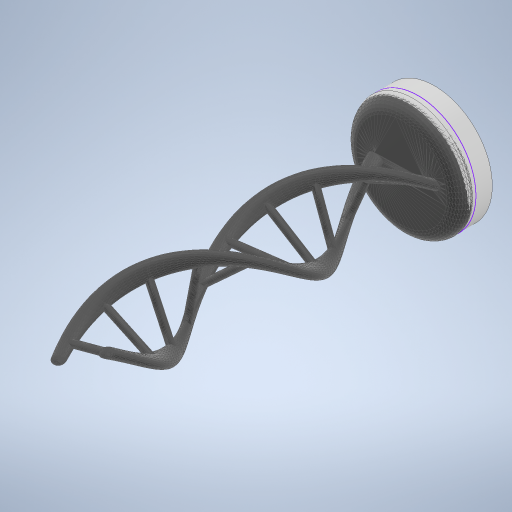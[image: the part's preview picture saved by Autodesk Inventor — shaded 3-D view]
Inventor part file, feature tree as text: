
AUTODESK INVENTOR PART (.ipt)
format: ipt  version: 2024.2 (Build 282272000, 272)  size: 821,248 bytes
history: native  units: mm
features: other x4, sketch x2, extrude x2, fillet x1
ambient origin geometry x8: Origin, YZ Plane, XZ Plane, XY Plane, X Axis, Y Axis, Z Axis, Center Point
bodies: Body1 (feature_tree)
feature tree (9):
  other  "Твердое тело1"
  other  "Double Helix DNA"
  sketch  "Эскиз1"
  extrude  "Выдавливание1"  Depth=10.0mm TaperAngle=0.0deg
  fillet  "Сопряжение1"  Radius=7.0mm
  other  "РабТочка1"
  extrude  "Выдавливание3"  Depth=3.0mm TaperAngle=0.0deg
  sketch  "Эскиз3"
  other  "ЭлементСетки1"
